# Revit family: DC_Holyoake_ElevatedTemperature_HCD-150-ET_13
name_source: partatom
category: Duct Accessories
revit_build: Autodesk Revit 2014 (Build: 20130308_1515(x64)
units: mm (PartAtom-declared; Revit-internal decimal feet)

## types (1)
- Variable Width & Height
    3D Visibility ON OFF = No
    Description = Elevated Temperature Control Dampers shall be Holyoake Low Leakage Model HCD-150-ET. Elevated Temperature Control Dampers shall be of 6063 T5 extruded aluminium construction with 150mm Flanged Frame incorporating pre-punched corner slots for Duct Flange mounting or Channel Frame suitable for fixing inside ductwork. Elevated Temperature Control Dampers shall incorporate single piece Airfoil Blades, fitted with high temperature (225 Degree C) self inflating edge seals and flexible aluminium side seals. Elevated Temperature Control Dampers shall be fitted with 11mm Hexagonal shafts and shall rotate in high temperature (210 Degree C) two piece nylon bearings.
    Holyoake Product Range = Holyoake Motorised Volume Control Damper Elevated Temperature
    Manufacturer = Holyoake
    Material Body = Holyoake-Aluminium
    Material Face = Holyoake-Aluminium
    Model = HCD-150-ET
    Static Pressure Max / sqm = 2000 Pa
    Static Pressure Min / sqm = 10 Pa
    Type Comments = Low Leakage Motorised Volume Control Damper
    URL = http://www.holyoake.com

## geometry (parser evidence)
native form markers: Blend x12, Extrusion x6, Sweep x3
no freeform markers — native parametric forms only
